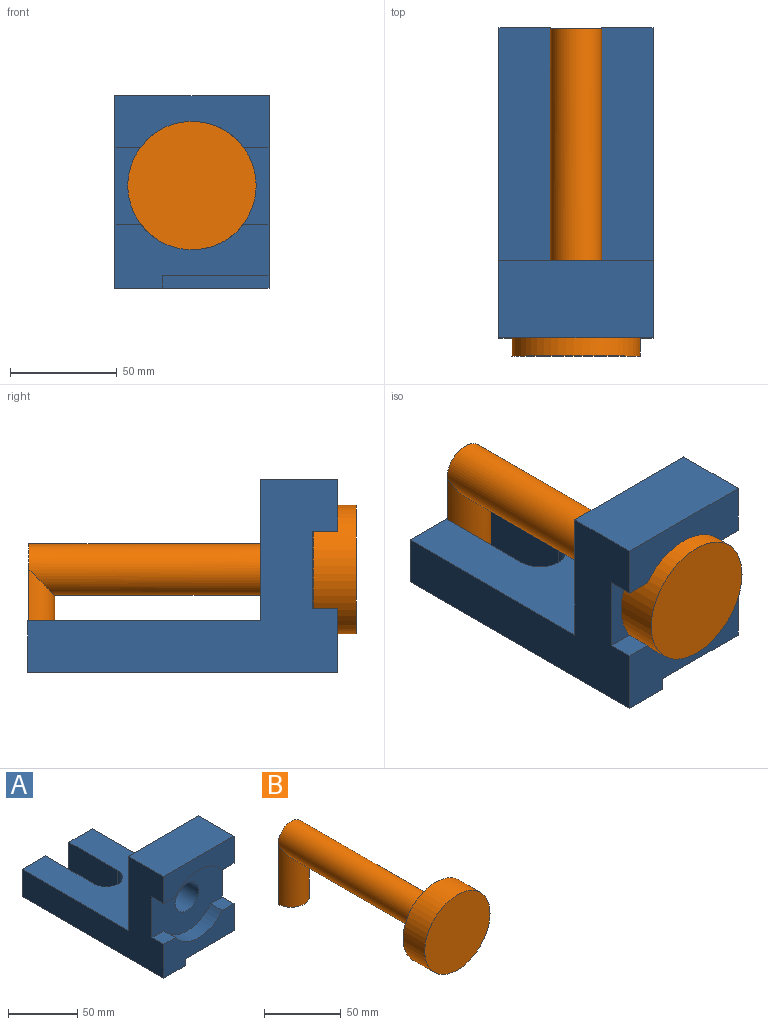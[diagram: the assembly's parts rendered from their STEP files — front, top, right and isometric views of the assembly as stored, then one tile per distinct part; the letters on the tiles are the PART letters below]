
ASSEMBLY  parts=2 mates=1
PART A: 24 faces, bbox 72x145x90 mm
  f0: plane 24.01x24mm, normal (0,1,0), area 576.3mm2, adj f1,f6,f19,f23
  f1: plane 145x72mm, normal (0,0,-1), area 5413.8mm2, adj f0,f2,f6,f7,f13,f18,f20,f21
  f2: plane 145x90mm, normal (1,0,0), area 4993.3mm2, adj f1,f3,f5,f8,f10,f11,f13,f15
  f3: plane 72x65.99mm, normal (0,1,0), area 4298.8mm2, adj f2,f6,f10,f17,f19
  f4: cylinder r=30mm len=48mm, axis (0,1,0), area 667.7mm2, adj f5,f11,f12,f13
  f5: plane 72x60mm, normal (0,-1,0), area 2944.7mm2, adj f2,f4,f6,f9,f11,f12,f14,f15
  f6: plane 145x90mm, normal (-1,0,0), area 5425.3mm2, adj f0,f1,f3,f5,f10,f12,f13,f14
  f7: plane 72x6mm, normal (1,0,0), area 432mm2, adj f1,f8,f13,f20
  f8: plane 72x50mm, normal (0,0,-1), area 3600mm2, adj f2,f7,f13,f20
  f9: cylinder r=30mm len=48mm, axis (0,1,0), area 667.7mm2, adj f5,f14,f15,f16
  f10: plane 72x36mm, normal (0,0,1), area 2592mm2, adj f2,f3,f6,f16
  f11: plane 12x12mm, normal (0,0,1), area 144mm2, adj f2,f4,f5,f13
  f12: plane 12x12mm, normal (0,0,1), area 144mm2, adj f4,f5,f6,f13
  f13: plane 72x30mm, normal (0,-1,0), area 1457.4mm2, adj f1,f2,f4,f6,f7,f8,f11,f12
  f14: plane 12x12mm, normal (0,0,-1), area 144mm2, adj f5,f6,f9,f16
  f15: plane 12x12mm, normal (0,0,-1), area 144mm2, adj f2,f5,f9,f16
  f16: plane 72x24mm, normal (0,-1,0), area 1325.4mm2, adj f2,f6,f9,f10,f14,f15
  f17: cylinder r=12mm len=24mm, axis (0,1,0), area 1809.6mm2, adj f3,f5
  f18: plane 24.01x24mm, normal (0,1,0), area 576.3mm2, adj f1,f2,f19,f22
  f19: plane 109x72mm, normal (0,0,1), area 6421.8mm2, adj f0,f2,f3,f6,f18,f21,f22,f23
  f20: plane 50x6mm, normal (0,-1,0), area 300mm2, adj f1,f2,f7,f8
  f21: cylinder r=12mm len=24.01mm, axis (0,0,1), area 905.2mm2, adj f1,f19,f22,f23
  f22: plane 50x24.01mm, normal (-1,0,0), area 1200.6mm2, adj f1,f18,f19,f21
  f23: plane 50x24.01mm, normal (1,0,0), area 1200.6mm2, adj f0,f1,f19,f21
PART B: 7 faces, bbox 60x153x78 mm
  f0: cylinder r=12mm len=133mm, axis (0,1,0), area 9740mm2, adj f1,f4,f6
  f1: plane 60x24mm, normal (0,1,0), area 1378.2mm2, adj f0,f5,f6
  f2: cylinder r=30mm len=60mm, axis (0,1,0), area 3769.9mm2, adj f3,f4
  f3: plane 60x60mm, normal (0,-1,0), area 2827.4mm2, adj f2
  f4: plane 60x60mm, normal (0,1,0), area 2375mm2, adj f0,f2
  f5: plane 24x12mm, normal (0,0,-1), area 226.2mm2, adj f1,f6
  f6: cylinder r=12mm len=48mm, axis (0,0,-1), area 1521.6mm2, adj f0,f1,f5
PLACE A t=(-9.8,-19.23,37.38)mm fixed
PLACE B t=(-9.8,22.77,37.38)mm
MATE slider B.f0 <-> A.f4  axis (0,1,0) through (-9.8,22.77,37.38)mm
